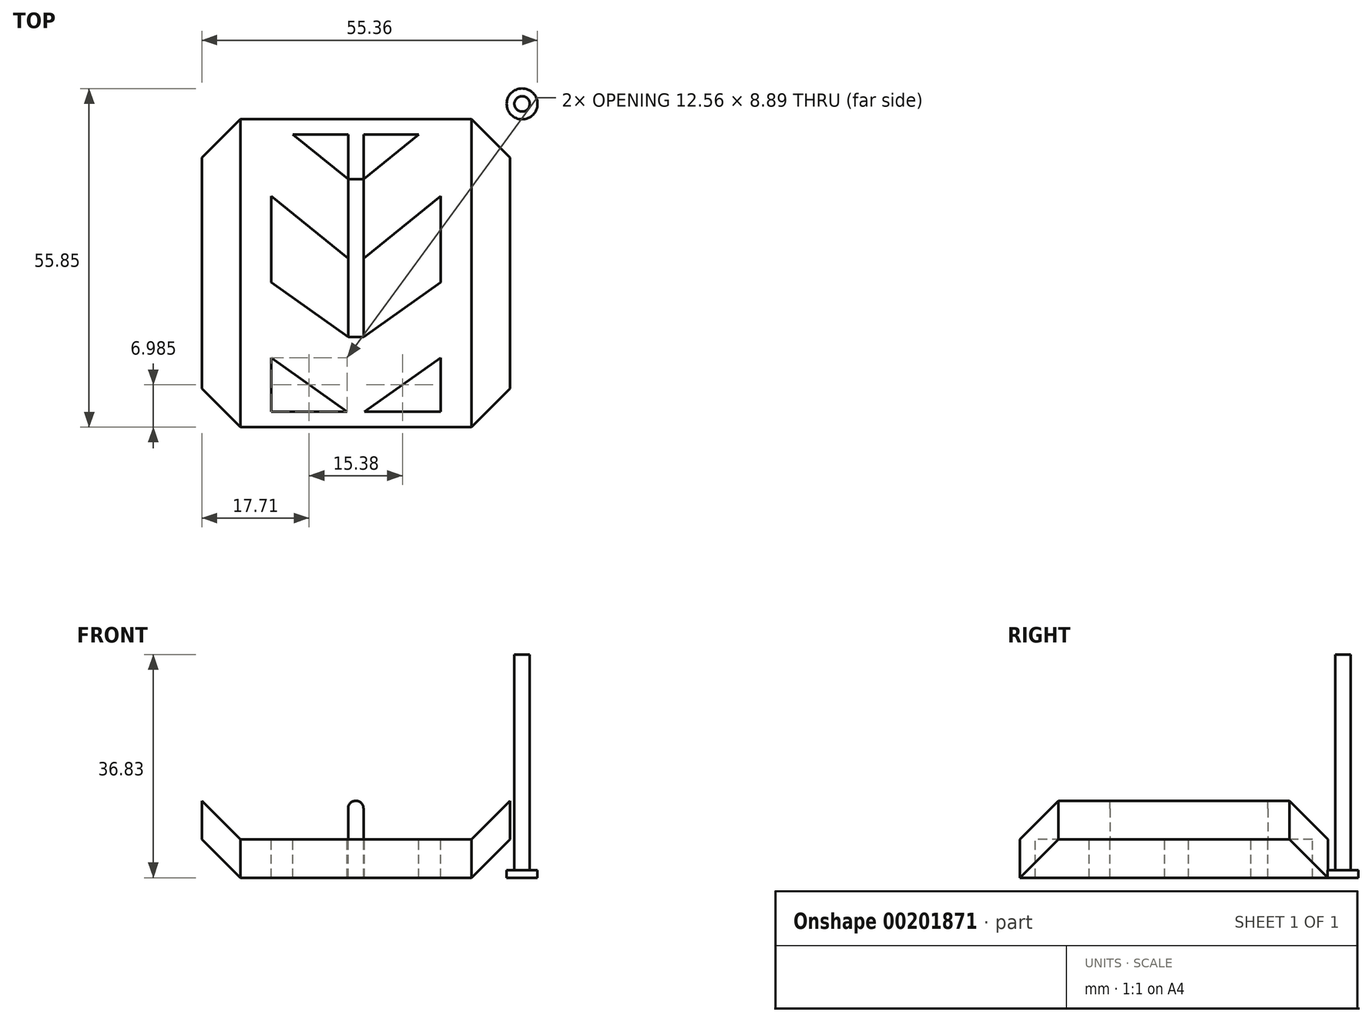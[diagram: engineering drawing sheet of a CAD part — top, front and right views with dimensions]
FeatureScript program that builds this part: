
annotation { "Feature Type Name" : "Feature", "Feature Type Description" : "" }
export const myFeature = defineFeature(function(context is Context, id is Id, definition is map)
    precondition{}
    {
        {
            var Q0;
            Q0=qCreatedBy(makeId("Top.planeOp"),FACE);
            var sketch = newSketch(context, id + "F0", { "sketchPlane" : qUnion([Q0])});
            skLineSegment(sketch, "E0.bottom", {"start": v(-19.05, 25.4) * mm, "end": v(19.05, 25.4) * mm});
            skLineSegment(sketch, "E0.top", {"start": v(-19.05, -25.4) * mm, "end": v(19.05, -25.4) * mm});
            skLineSegment(sketch, "E0.left", {"start": v(-19.05, 25.4) * mm, "end": v(-19.05, -25.4) * mm});
            skLineSegment(sketch, "E0.right", {"start": v(19.05, 25.4) * mm, "end": v(19.05, -25.4) * mm});
            skPoint(sketch, "E0.middle", {"position": v(0, 0) * mm});
            skSolve(sketch);
        }
        {
            var Q0;
            Q0=makeQuery(id+"F0.imprint","IMPRINT",FACE,{"disambiguationData":[TD([[makeQuery(id+"F0.imprint","IMPRINT",EDGE,{"derivedFrom":sQuery(id+"F0.wireOp",EDGE,"E0.bottom")}),-1.0]])]});
            extrude(context, id + "F1", {"entities" : qUnion([Q0]), "depth" : 6.35 * mm});
        }
        {
            var Q0;
            Q0=makeQuery(id+"F1.opExtrude","SWEPT_FACE",FACE,{"disambiguationData":[OSD([sQuery(id+"F0.wireOp",EDGE,"E0.top")])]});
            var sketch = newSketch(context, id + "F2", { "sketchPlane" : qUnion([Q0])});
            skLineSegment(sketch, "E1", {"start": v(-19.05, 6.35) * mm, "end": v(-25.4, 12.7) * mm});
            skLineSegment(sketch, "E2", {"start": v(-19.05, 0) * mm, "end": v(-25.4, 6.35) * mm});
            skLineSegment(sketch, "E3", {"start": v(-25.4, 6.35) * mm, "end": v(-25.4, 12.7) * mm});
            skLineSegment(sketch, "E4", {"start": v(-19.05, 6.35) * mm, "end": v(-19.05, 0) * mm});
            skSolve(sketch);
        }
        {
            var Q0;
            Q0 = qSketchRegion(id + "F2", true);
            var Q1;
            Q1=makeQuery(id+"F1.opExtrude","CAP_VERTEX",VERTEX,{"disambiguationData":[OSD([sQuery(id+"F0.wireOp",EDGE,"E0.bottom"),sQuery(id+"F0.wireOp",EDGE,"E0.left")])],"isStart":false});
            extrude(context, id + "F3", {"entities" : qUnion([Q0]), "operationType" : NewBodyOperationType.ADD, "endBound" : BoundingType.UP_TO_VERTEX, "oppositeDirection" : true, "endBoundEntityVertex" : qUnion([Q1]), "depth" : 25.4 * mm});
        }
        {
            var Q0;
            Q0=qCreatedBy(makeId("Right.planeOp"),FACE);
            var sketch = newSketch(context, id + "F4", { "sketchPlane" : qUnion([Q0])});
            skLineSegment(sketch, "E5.0.1", {"start": v(25.4, 0) * mm, "end": v(-25.4, 0) * mm});
            skLineSegment(sketch, "E6.0.0", {"start": v(-25.4, 0) * mm, "end": v(25.4, 0) * mm});
            skLineSegment(sketch, "E6.0.2", {"start": v(25.4, 6.35) * mm, "end": v(-25.4, 6.35) * mm});
            skLineSegment(sketch, "E6.0.3", {"start": v(-25.4, 6.35) * mm, "end": v(-25.4, 0) * mm});
            skLineSegment(sketch, "E7.bottom", {"start": v(-25.4, 0) * mm, "end": v(-31.75, 0) * mm});
            skLineSegment(sketch, "E7.top", {"start": v(-25.4, 6.35) * mm, "end": v(-31.75, 6.35) * mm});
            skLineSegment(sketch, "E7.left", {"start": v(-25.4, 0) * mm, "end": v(-25.4, 6.35) * mm});
            skLineSegment(sketch, "E7.right", {"start": v(-31.75, 0) * mm, "end": v(-31.75, 6.35) * mm});
            skPoint(sketch, "E8", {"position": v(-31.75, 3.18) * mm});
            skLineSegment(sketch, "E9", {"start": v(0, 0) * mm, "end": v(0, 6.35) * mm});
            skLineSegment(sketch, "E10.MirrorCS", {"start": v(-25.4, 6.35) * mm, "end": v(25.4, 6.35) * mm});
            skArc(sketch, "E11", {"start": v(-28.57, 6.35) * mm, "mid": v(-31.75, 3.18) * mm, "end": v(-28.57, 0) * mm});
            skCircle(sketch, "E12", {"center": v(-28.57, 3.18) * mm, "radius": 1.59 * mm});
            skLineSegment(sketch, "E13.MirrorCS", {"start": v(25.4, 6.35) * mm, "end": v(25.4, 0) * mm});
            skLineSegment(sketch, "E14.MirrorCS", {"start": v(25.4, 6.35) * mm, "end": v(31.75, 6.35) * mm});
            skPoint(sketch, "E15.MirrorP", {"position": v(31.75, 3.17) * mm});
            skLineSegment(sketch, "E16.MirrorCS", {"start": v(25.4, 0) * mm, "end": v(25.4, 6.35) * mm});
            skCircle(sketch, "E17.MirrorC", {"center": v(28.58, 3.17) * mm, "radius": 1.59 * mm});
            skLineSegment(sketch, "E18.MirrorCS", {"start": v(31.75, 0) * mm, "end": v(31.75, 6.35) * mm});
            skLineSegment(sketch, "E19.MirrorCS", {"start": v(25.4, 0) * mm, "end": v(31.75, 0) * mm});
            skArc(sketch, "E20.MirrorCS", {"start": v(28.58, 6.35) * mm, "mid": v(31.75, 3.17) * mm, "end": v(28.57, 0) * mm});
            skSolve(sketch);
        }
        {
            var Q0;
            {var subQ0=sQuery(id+"F4.wireOp",EDGE,"E7.left");Q0=makeQuery(id+"F4.imprint","IMPRINT",FACE,{"disambiguationData":[TD([[makeQuery(id+"F4.imprint","IMPRINT",EDGE,{"derivedFrom":subQ0}),-1.0]])]});}
            var Q1;
            {var subQ0=sQuery(id+"F4.wireOp",EDGE,"E9");Q1=makeQuery(id+"F4.imprint","IMPRINT",FACE,{"disambiguationData":[TD([[makeQuery(id+"F4.imprint","IMPRINT",EDGE,{"derivedFrom":subQ0}),-1.0]])]});}
            var Q2;
            {var subQ4=sQuery(id+"F4.wireOp",EDGE,"E7.left");Q2=makeQuery(id+"F4.imprint","IMPRINT",FACE,{"disambiguationData":[TD([[makeQuery(id+"F4.imprint","IMPRINT",EDGE,{"derivedFrom":subQ4}),1.0]])]});}
            var Q3;
            {var subQ1=sQuery(id+"F4.wireOp",EDGE,"E16.MirrorCS");Q3=makeQuery(id+"F4.imprint","IMPRINT",FACE,{"disambiguationData":[TD([[makeQuery(id+"F4.imprint","IMPRINT",EDGE,{"derivedFrom":subQ1}),-1.0]])]});}
            extrude(context, id + "F5", {"entities" : qUnion([Q0, Q1, Q2, Q3]), "operationType" : NewBodyOperationType.ADD, "endBound" : BoundingType.SYMMETRIC, "depth" : 38.1 * mm});
        }
        {
            var Q0;
            Q0=makeQuery(id+"F5.boolean.opBoolean","MERGE",FACE,{"derivedFrom":[makeQuery(id+"F1.opExtrude","CAP_FACE",FACE,{"disambiguationData":[OSD([sQuery(id+"F0.wireOp",EDGE,"E0.bottom"),sQuery(id+"F0.wireOp",EDGE,"E0.top"),sQuery(id+"F0.wireOp",EDGE,"E0.left"),sQuery(id+"F0.wireOp",EDGE,"E0.right")])],"isStart":false}),makeQuery(id+"F5.opExtrude","SWEPT_FACE",FACE,{"disambiguationData":[OSD([sQuery(id+"F4.wireOp",EDGE,"E7.top"),sQuery(id+"F4.wireOp",EDGE,"2de5de97-5122-4665-80c7-dcd164dd88c95.MirrorCS"),sQuery(id+"F4.wireOp",EDGE,"E10.MirrorCS")])]})]});
            var sketch = newSketch(context, id + "F6", { "sketchPlane" : qUnion([Q0])});
            skLineSegment(sketch, "E21.bottom", {"start": v(-6.35, 31.75) * mm, "end": v(6.35, 31.75) * mm});
            skLineSegment(sketch, "E21.top", {"start": v(-6.35, -31.75) * mm, "end": v(6.35, -31.75) * mm});
            skLineSegment(sketch, "E21.left", {"start": v(-6.35, 31.75) * mm, "end": v(-6.35, -31.75) * mm});
            skLineSegment(sketch, "E21.right", {"start": v(6.35, 31.75) * mm, "end": v(6.35, -31.75) * mm});
            skPoint(sketch, "E21.middle", {"position": v(0, 0) * mm});
            skLineSegment(sketch, "E22.bottom", {"start": v(-19.05, 31.75) * mm, "end": v(19.05, 31.75) * mm});
            skLineSegment(sketch, "E22.top", {"start": v(-19.05, -31.75) * mm, "end": v(19.05, -31.75) * mm});
            skLineSegment(sketch, "E22.left", {"start": v(-19.05, 31.75) * mm, "end": v(-19.05, -31.75) * mm});
            skLineSegment(sketch, "E22.right", {"start": v(19.05, 31.75) * mm, "end": v(19.05, -31.75) * mm});
            skLineSegment(sketch, "E23.bottom", {"start": v(-19.05, 25.4) * mm, "end": v(19.05, 25.4) * mm});
            skLineSegment(sketch, "E23.top", {"start": v(-19.05, -25.4) * mm, "end": v(19.05, -25.4) * mm});
            skLineSegment(sketch, "E23.left", {"start": v(-19.05, 25.4) * mm, "end": v(-19.05, -25.4) * mm});
            skLineSegment(sketch, "E23.right", {"start": v(19.05, 25.4) * mm, "end": v(19.05, -25.4) * mm});
            skLineSegment(sketch, "E24.bottom", {"start": v(5.84, -25.4) * mm, "end": v(-5.84, -25.4) * mm});
            skLineSegment(sketch, "E24.top", {"start": v(5.84, -31.75) * mm, "end": v(-5.84, -31.75) * mm});
            skLineSegment(sketch, "E24.left", {"start": v(5.84, -25.4) * mm, "end": v(5.84, -31.75) * mm});
            skLineSegment(sketch, "E24.right", {"start": v(-5.84, -25.4) * mm, "end": v(-5.84, -31.75) * mm});
            skSolve(sketch);
        }
        {
            var Q0;
            {var subQ0=sQuery(id+"F6.wireOp",EDGE,"E22.bottom");var subQ1=sQuery(id+"F6.wireOp",EDGE,"E21.left");var subQ2=makeQuery(id+"F6.imprint","INTERSECT",VERTEX,{"derivedFrom":[subQ1,subQ0]});Q0=makeQuery(id+"F6.imprint","IMPRINT",FACE,{"disambiguationData":[TD([[makeQuery(id+"F6.imprint","IMPRINT",EDGE,{"disambiguationData":[TD([[subQ2,-1.0]])],"derivedFrom":subQ0}),-1.0]])]});}
            var Q1;
            {var subQ0=sQuery(id+"F6.wireOp",EDGE,"E23.bottom");var subQ1=sQuery(id+"F6.wireOp",EDGE,"E21.left");var subQ2=makeQuery(id+"F6.imprint","INTERSECT",VERTEX,{"derivedFrom":[subQ1,subQ0]});Q1=makeQuery(id+"F6.imprint","IMPRINT",FACE,{"disambiguationData":[TD([[makeQuery(id+"F6.imprint","IMPRINT",EDGE,{"disambiguationData":[TD([[subQ2,-1.0]])],"derivedFrom":subQ0}),1.0]])]});}
            var Q2;
            {var subQ0=sQuery(id+"F6.wireOp",EDGE,"E22.top");var subQ1=sQuery(id+"F6.wireOp",EDGE,"E21.right");var subQ2=makeQuery(id+"F6.imprint","INTERSECT",VERTEX,{"derivedFrom":[subQ1,subQ0]});Q2=makeQuery(id+"F6.imprint","IMPRINT",FACE,{"disambiguationData":[TD([[makeQuery(id+"F6.imprint","IMPRINT",EDGE,{"disambiguationData":[TD([[subQ2,-1.0]])],"derivedFrom":subQ0}),1.0]])]});}
            var Q3;
            {var subQ0=sQuery(id+"F6.wireOp",EDGE,"E23.top");var subQ1=sQuery(id+"F6.wireOp",EDGE,"E21.right");var subQ2=makeQuery(id+"F6.imprint","INTERSECT",VERTEX,{"derivedFrom":[subQ1,subQ0]});Q3=makeQuery(id+"F6.imprint","IMPRINT",FACE,{"disambiguationData":[TD([[makeQuery(id+"F6.imprint","IMPRINT",EDGE,{"disambiguationData":[TD([[subQ2,-1.0]])],"derivedFrom":subQ1}),1.0]])]});}
            var Q4;
            {var subQ0=sQuery(id+"F6.wireOp",EDGE,"E23.top");var subQ1=sQuery(id+"F6.wireOp",EDGE,"E21.right");var subQ2=makeQuery(id+"F6.imprint","INTERSECT",VERTEX,{"derivedFrom":[subQ1,subQ0]});Q4=makeQuery(id+"F6.imprint","IMPRINT",FACE,{"disambiguationData":[TD([[makeQuery(id+"F6.imprint","IMPRINT",EDGE,{"disambiguationData":[TD([[subQ2,-1.0]])],"derivedFrom":subQ1}),-1.0]])]});}
            var Q5;
            {var subQ0=sQuery(id+"F6.wireOp",EDGE,"E22.top");var subQ1=sQuery(id+"F6.wireOp",EDGE,"E21.right");var subQ2=makeQuery(id+"F6.imprint","INTERSECT",VERTEX,{"derivedFrom":[subQ1,subQ0]});Q5=makeQuery(id+"F6.imprint","IMPRINT",FACE,{"disambiguationData":[TD([[makeQuery(id+"F6.imprint","IMPRINT",EDGE,{"disambiguationData":[TD([[subQ2,1.0]])],"derivedFrom":subQ1}),-1.0]])]});}
            var Q6;
            {var subQ0=sQuery(id+"F6.wireOp",EDGE,"E22.top");var subQ1=sQuery(id+"F6.wireOp",EDGE,"E21.left");var subQ2=makeQuery(id+"F6.imprint","INTERSECT",VERTEX,{"derivedFrom":[subQ1,subQ0]});Q6=makeQuery(id+"F6.imprint","IMPRINT",FACE,{"disambiguationData":[TD([[makeQuery(id+"F6.imprint","IMPRINT",EDGE,{"disambiguationData":[TD([[subQ2,1.0]])],"derivedFrom":subQ0}),1.0]])]});}
            var Q7;
            {var subQ0=sQuery(id+"F6.wireOp",EDGE,"E23.top");var subQ1=sQuery(id+"F6.wireOp",EDGE,"E21.left");var subQ2=makeQuery(id+"F6.imprint","INTERSECT",VERTEX,{"derivedFrom":[subQ1,subQ0]});Q7=makeQuery(id+"F6.imprint","IMPRINT",FACE,{"disambiguationData":[TD([[makeQuery(id+"F6.imprint","IMPRINT",EDGE,{"disambiguationData":[TD([[subQ2,-1.0]])],"derivedFrom":subQ1}),-1.0]])]});}
            var Q8;
            {var subQ0=sQuery(id+"F6.wireOp",EDGE,"E23.top");var subQ1=sQuery(id+"F6.wireOp",EDGE,"E21.left");var subQ2=makeQuery(id+"F6.imprint","INTERSECT",VERTEX,{"derivedFrom":[subQ1,subQ0]});Q8=makeQuery(id+"F6.imprint","IMPRINT",FACE,{"disambiguationData":[TD([[makeQuery(id+"F6.imprint","IMPRINT",EDGE,{"disambiguationData":[TD([[subQ2,-1.0]])],"derivedFrom":subQ1}),1.0]])]});}
            var Q9;
            {var subQ0=sQuery(id+"F6.wireOp",EDGE,"E22.top");var subQ1=sQuery(id+"F6.wireOp",EDGE,"E21.left");var subQ2=makeQuery(id+"F6.imprint","INTERSECT",VERTEX,{"derivedFrom":[subQ1,subQ0]});Q9=makeQuery(id+"F6.imprint","IMPRINT",FACE,{"disambiguationData":[TD([[makeQuery(id+"F6.imprint","IMPRINT",EDGE,{"disambiguationData":[TD([[subQ2,1.0]])],"derivedFrom":subQ1}),1.0]])]});}
            extrude(context, id + "F7", {"entities" : qUnion([Q0, Q1, Q2, Q3, Q4, Q5, Q6, Q7, Q8, Q9]), "operationType" : NewBodyOperationType.REMOVE, "oppositeDirection" : true, "depth" : 25.4 * mm});
        }
        {
            var Q0;
            Q0=makeQuery(id+"F5.boolean.opBoolean","MERGE",FACE,{"derivedFrom":[makeQuery(id+"F1.opExtrude","CAP_FACE",FACE,{"disambiguationData":[OSD([sQuery(id+"F0.wireOp",EDGE,"E0.bottom"),sQuery(id+"F0.wireOp",EDGE,"E0.top"),sQuery(id+"F0.wireOp",EDGE,"E0.left"),sQuery(id+"F0.wireOp",EDGE,"E0.right")])],"isStart":false}),makeQuery(id+"F5.opExtrude","SWEPT_FACE",FACE,{"disambiguationData":[OSD([sQuery(id+"F4.wireOp",EDGE,"E7.top"),sQuery(id+"F4.wireOp",EDGE,"2de5de97-5122-4665-80c7-dcd164dd88c95.MirrorCS"),sQuery(id+"F4.wireOp",EDGE,"E10.MirrorCS")])]})]});
            var sketch = newSketch(context, id + "F8", { "sketchPlane" : qUnion([Q0])});
            skLineSegment(sketch, "E25", {"start": v(-19.05, 25.4) * mm, "end": v(-35.68, 25.4) * mm});
            skLineSegment(sketch, "E26", {"start": v(-19.05, 25.4) * mm, "end": v(-35.36, 9.09) * mm});
            skLineSegment(sketch, "E27", {"start": v(-19.05, -25.4) * mm, "end": v(-35, -9.44) * mm});
            skLineSegment(sketch, "E28", {"start": v(-19.05, -25.4) * mm, "end": v(-34.7, -25.4) * mm});
            skLineSegment(sketch, "E29", {"start": v(-35.68, 25.4) * mm, "end": v(-34.7, -25.4) * mm});
            skSolve(sketch);
        }
        {
            var Q0;
            {var subQ0=sQuery(id+"F8.wireOp",EDGE,"E25");Q0=makeQuery(id+"F8.imprint","IMPRINT",FACE,{"disambiguationData":[TD([[makeQuery(id+"F8.imprint","IMPRINT",EDGE,{"derivedFrom":subQ0}),1.0]])]});}
            var Q1;
            {var subQ0=sQuery(id+"F8.wireOp",EDGE,"E27");Q1=makeQuery(id+"F8.imprint","IMPRINT",FACE,{"disambiguationData":[TD([[makeQuery(id+"F8.imprint","IMPRINT",EDGE,{"derivedFrom":subQ0}),1.0]])]});}
            extrude(context, id + "F9", {"entities" : qUnion([Q0, Q1]), "operationType" : NewBodyOperationType.REMOVE, "endBound" : BoundingType.SYMMETRIC, "depth" : 25.4 * mm});
        }
        {
            var Q0;
            Q0=makeQuery(id+"F5.boolean.opBoolean","MERGE",FACE,{"derivedFrom":[makeQuery(id+"F1.opExtrude","SWEPT_FACE",FACE,{"disambiguationData":[OSD([sQuery(id+"F0.wireOp",EDGE,"E0.right")])]}),makeQuery(id+"F5.opExtrude","CAP_FACE",FACE,{"disambiguationData":[OSD([sQuery(id+"F4.wireOp",EDGE,"E7.bottom"),sQuery(id+"F4.wireOp",EDGE,"E7.top"),sQuery(id+"F4.wireOp",EDGE,"E7.right"),sQuery(id+"F4.wireOp",EDGE,"JeROhu54-lmU2-9Cnl-GVbt-ESwWcb09rHdF"),sQuery(id+"F4.wireOp",EDGE,"2de5de97-5122-4665-80c7-dcd164dd88c94.MirrorCS"),sQuery(id+"F4.wireOp",EDGE,"2de5de97-5122-4665-80c7-dcd164dd88c95.MirrorCS"),sQuery(id+"F4.wireOp",EDGE,"2de5de97-5122-4665-80c7-dcd164dd88c96.MirrorCS"),sQuery(id+"F4.wireOp",EDGE,"E5.0.1"),sQuery(id+"F4.wireOp",EDGE,"2de5de97-5122-4665-80c7-dcd164dd88c99.MirrorC"),sQuery(id+"F4.wireOp",EDGE,"E10.MirrorCS")])],"isStart":false})]});
            cPlane(context, id + "F10", {"entities" : qUnion([Q0]), "cplaneType" : CPlaneType.OFFSET, "offset" : 19.05 * mm, "oppositeDirection" : true, "width" : 152.4 * mm, "height" : 152.4 * mm});
        }
        {
            var Q0;
            Q0=makeQuery(id+"F1.opExtrude","SWEPT_BODY",BODY,{"disambiguationData":[OSD([sQuery(id+"F0.wireOp",EDGE,"E0.bottom"),sQuery(id+"F0.wireOp",EDGE,"E0.top"),sQuery(id+"F0.wireOp",EDGE,"E0.left"),sQuery(id+"F0.wireOp",EDGE,"E0.right")])]});
            var Q1;
            Q1=qCreatedBy(id+"F10.planeOp",FACE);
            mirror(context, id + "F11", {"operationType" : NewBodyOperationType.ADD, "entities" : qUnion([Q0]), "mirrorPlane" : qUnion([Q1])});
        }
        {
            var Q0;
            Q0=makeQuery(id+"F5.boolean.opBoolean","MERGE",FACE,{"derivedFrom":[makeQuery(id+"F1.opExtrude","CAP_FACE",FACE,{"disambiguationData":[OSD([sQuery(id+"F0.wireOp",EDGE,"E0.bottom"),sQuery(id+"F0.wireOp",EDGE,"E0.top"),sQuery(id+"F0.wireOp",EDGE,"E0.left"),sQuery(id+"F0.wireOp",EDGE,"E0.right")])],"isStart":false}),makeQuery(id+"F5.opExtrude","SWEPT_FACE",FACE,{"disambiguationData":[OSD([sQuery(id+"F4.wireOp",EDGE,"E7.top"),sQuery(id+"F4.wireOp",EDGE,"E14.MirrorCS"),sQuery(id+"F4.wireOp",EDGE,"E6.0.2")])]})]});
            var sketch = newSketch(context, id + "F12", { "sketchPlane" : qUnion([Q0])});
            skLineSegment(sketch, "E30.bottom", {"start": v(-13.97, 22.86) * mm, "end": v(13.97, 22.86) * mm});
            skLineSegment(sketch, "E30.top", {"start": v(-13.97, -22.86) * mm, "end": v(13.97, -22.86) * mm});
            skLineSegment(sketch, "E30.left", {"start": v(-13.97, 22.86) * mm, "end": v(-13.97, -22.86) * mm});
            skLineSegment(sketch, "E30.right", {"start": v(13.97, 22.86) * mm, "end": v(13.97, -22.86) * mm});
            skLineSegment(sketch, "E31.bottom", {"start": v(-1.27, 22.86) * mm, "end": v(1.27, 22.86) * mm});
            skLineSegment(sketch, "E31.top", {"start": v(-1.27, -22.86) * mm, "end": v(1.27, -22.86) * mm});
            skLineSegment(sketch, "E31.left", {"start": v(-1.27, 22.86) * mm, "end": v(-1.27, -22.86) * mm});
            skLineSegment(sketch, "E31.right", {"start": v(1.27, 22.86) * mm, "end": v(1.27, -22.86) * mm});
            skLineSegment(sketch, "E32", {"start": v(-13.97, 0) * mm, "end": v(13.97, 0) * mm});
            skLineSegment(sketch, "E33", {"start": v(-13.97, 22.86) * mm, "end": v(-13.97, 0) * mm});
            skLineSegment(sketch, "E34", {"start": v(-13.97, 0) * mm, "end": v(-13.97, -22.86) * mm});
            skLineSegment(sketch, "E35", {"start": v(-13.97, 11.43) * mm, "end": v(13.97, 11.43) * mm, "construction": true});
            skLineSegment(sketch, "E36", {"start": v(-13.97, -11.43) * mm, "end": v(13.97, -11.43) * mm, "construction": true});
            skLineSegment(sketch, "E37", {"start": v(-10.38, 22.86) * mm, "end": v(-1.27, 15.5) * mm});
            skLineSegment(sketch, "E38", {"start": v(-13.97, 12.7) * mm, "end": v(-1.27, 2.43) * mm});
            skLineSegment(sketch, "E39", {"start": v(-13.97, -1.52) * mm, "end": v(-1.27, -10.51) * mm});
            skLineSegment(sketch, "E40", {"start": v(-13.97, -13.97) * mm, "end": v(-1.41, -22.86) * mm});
            skLineSegment(sketch, "E41", {"start": v(0, 22.86) * mm, "end": v(0, 21.42) * mm});
            skPoint(sketch, "E41.endSnap0", {"position": v(0, 22.86) * mm});
            skLineSegment(sketch, "E42.MirrorCS", {"start": v(10.38, 22.86) * mm, "end": v(1.27, 15.5) * mm});
            skLineSegment(sketch, "E43.MirrorCS", {"start": v(13.97, -13.97) * mm, "end": v(1.41, -22.86) * mm});
            skLineSegment(sketch, "E44.MirrorCS", {"start": v(13.97, 12.7) * mm, "end": v(1.27, 2.43) * mm});
            skLineSegment(sketch, "E45.MirrorCS", {"start": v(13.97, -1.52) * mm, "end": v(1.27, -10.51) * mm});
            skLineSegment(sketch, "E46.MirrorCS", {"start": v(13.97, 22.86) * mm, "end": v(13.97, 0) * mm});
            skLineSegment(sketch, "E47.MirrorCS", {"start": v(13.97, 0) * mm, "end": v(13.97, -22.86) * mm});
            skSolve(sketch);
        }
        {
            var Q0;
            {var subQ3=sQuery(id+"F12.wireOp",EDGE,"E37");Q0=makeQuery(id+"F12.imprint","IMPRINT",FACE,{"disambiguationData":[TD([[makeQuery(id+"F12.imprint","IMPRINT",EDGE,{"derivedFrom":subQ3}),1.0]])]});}
            var Q1;
            {var subQ3=sQuery(id+"F12.wireOp",EDGE,"E42.MirrorCS");Q1=makeQuery(id+"F12.imprint","IMPRINT",FACE,{"disambiguationData":[TD([[makeQuery(id+"F12.imprint","IMPRINT",EDGE,{"derivedFrom":subQ3}),-1.0]])]});}
            var Q2;
            {var subQ0=sQuery(id+"F12.wireOp",EDGE,"E39");Q2=makeQuery(id+"F12.imprint","IMPRINT",FACE,{"disambiguationData":[TD([[makeQuery(id+"F12.imprint","IMPRINT",EDGE,{"derivedFrom":subQ0}),1.0]])]});}
            var Q3;
            {var subQ5=sQuery(id+"F12.wireOp",EDGE,"E45.MirrorCS");Q3=makeQuery(id+"F12.imprint","IMPRINT",FACE,{"disambiguationData":[TD([[makeQuery(id+"F12.imprint","IMPRINT",EDGE,{"derivedFrom":subQ5}),-1.0]])]});}
            var Q4;
            {var subQ3=sQuery(id+"F12.wireOp",EDGE,"E43.MirrorCS");Q4=makeQuery(id+"F12.imprint","IMPRINT",FACE,{"disambiguationData":[TD([[makeQuery(id+"F12.imprint","IMPRINT",EDGE,{"derivedFrom":subQ3}),1.0]])]});}
            var Q5;
            {var subQ3=sQuery(id+"F12.wireOp",EDGE,"E40");Q5=makeQuery(id+"F12.imprint","IMPRINT",FACE,{"disambiguationData":[TD([[makeQuery(id+"F12.imprint","IMPRINT",EDGE,{"derivedFrom":subQ3}),-1.0]])]});}
            var Q6;
            {var subQ0=sQuery(id+"F12.wireOp",EDGE,"E38");Q6=makeQuery(id+"F12.imprint","IMPRINT",FACE,{"disambiguationData":[TD([[makeQuery(id+"F12.imprint","IMPRINT",EDGE,{"derivedFrom":subQ0}),-1.0]])]});}
            var Q7;
            {var subQ5=sQuery(id+"F12.wireOp",EDGE,"E44.MirrorCS");Q7=makeQuery(id+"F12.imprint","IMPRINT",FACE,{"disambiguationData":[TD([[makeQuery(id+"F12.imprint","IMPRINT",EDGE,{"derivedFrom":subQ5}),1.0]])]});}
            extrude(context, id + "F13", {"entities" : qUnion([Q0, Q1, Q2, Q3, Q4, Q5, Q6, Q7]), "operationType" : NewBodyOperationType.REMOVE, "endBound" : BoundingType.THROUGH_ALL, "oppositeDirection" : true, "depth" : 25.4 * mm});
        }
        {
            var Q0;
            Q0=makeQuery(id+"F5.boolean.opBoolean","MERGE",FACE,{"derivedFrom":[makeQuery(id+"F1.opExtrude","CAP_FACE",FACE,{"disambiguationData":[OSD([sQuery(id+"F0.wireOp",EDGE,"E0.bottom"),sQuery(id+"F0.wireOp",EDGE,"E0.top"),sQuery(id+"F0.wireOp",EDGE,"E0.left"),sQuery(id+"F0.wireOp",EDGE,"E0.right")])],"isStart":false}),makeQuery(id+"F5.opExtrude","SWEPT_FACE",FACE,{"disambiguationData":[OSD([sQuery(id+"F4.wireOp",EDGE,"E7.top"),sQuery(id+"F4.wireOp",EDGE,"E14.MirrorCS"),sQuery(id+"F4.wireOp",EDGE,"E6.0.2")])]})]});
            var sketch = newSketch(context, id + "F14", { "sketchPlane" : qUnion([Q0])});
            skLineSegment(sketch, "E48.bottom", {"start": v(-1.27, 15.5) * mm, "end": v(1.27, 15.5) * mm});
            skLineSegment(sketch, "E48.top", {"start": v(-1.27, -10.51) * mm, "end": v(1.27, -10.51) * mm});
            skLineSegment(sketch, "E48.left", {"start": v(-1.27, 15.5) * mm, "end": v(-1.27, -10.51) * mm});
            skLineSegment(sketch, "E48.right", {"start": v(1.27, 15.5) * mm, "end": v(1.27, -10.51) * mm});
            skSolve(sketch);
        }
        {
            var Q0;
            Q0 = qSketchRegion(id + "F14", true);
            extrude(context, id + "F15", {"entities" : qUnion([Q0]), "operationType" : NewBodyOperationType.ADD, "depth" : 6.35 * mm});
        }
        {
            var Q0;
            Q0=makeQuery(id+"F15.opExtrude","CAP_EDGE",EDGE,{"disambiguationData":[OSD([sQuery(id+"F14.wireOp",EDGE,"E48.left")])],"isStart":false});
            var Q1;
            Q1=makeQuery(id+"F15.opExtrude","CAP_EDGE",EDGE,{"disambiguationData":[OSD([sQuery(id+"F14.wireOp",EDGE,"E48.right")])],"isStart":false});
            fillet(context, id + "F16", {"entities" : qUnion([Q0, Q1]), "radius" : 1.27 * mm, "tangentPropagation" : true, "allowEdgeOverflow" : false});
        }
        {
            var Q0;
            Q0=makeQuery(id+"F0.imprint","IMPRINT",FACE,{"disambiguationData":[TD([[makeQuery(id+"F0.imprint","IMPRINT",EDGE,{"derivedFrom":sQuery(id+"F0.wireOp",EDGE,"E0.bottom")}),-1.0]])]});
            var sketch = newSketch(context, id + "F17", { "sketchPlane" : qUnion([Q0])});
            skCircle(sketch, "E49", {"center": v(27.42, 27.91) * mm, "radius": 2.54 * mm});
            skSolve(sketch);
        }
        {
            var Q0;
            Q0=makeQuery(id+"F17.imprint","IMPRINT",FACE,{"disambiguationData":[TD([[makeQuery(id+"F17.imprint","IMPRINT",EDGE,{"derivedFrom":sQuery(id+"F17.wireOp",EDGE,"E49")}),1.0]])]});
            extrude(context, id + "F18", {"entities" : qUnion([Q0]), "depth" : 1.27 * mm});
        }
        {
            var Q0;
            Q0=makeQuery(id+"F18.opExtrude","CAP_FACE",FACE,{"disambiguationData":[OSD([sQuery(id+"F17.wireOp",EDGE,"E49")])],"isStart":false});
            var sketch = newSketch(context, id + "F19", { "sketchPlane" : qUnion([Q0])});
            skCircle(sketch, "E50", {"center": v(27.42, 27.91) * mm, "radius": 1.27 * mm});
            skSolve(sketch);
        }
        {
            var Q0;
            Q0 = qSketchRegion(id + "F19", true);
            extrude(context, id + "F20", {"entities" : qUnion([Q0]), "operationType" : NewBodyOperationType.ADD, "depth" : 35.56 * mm});
        }
    });
